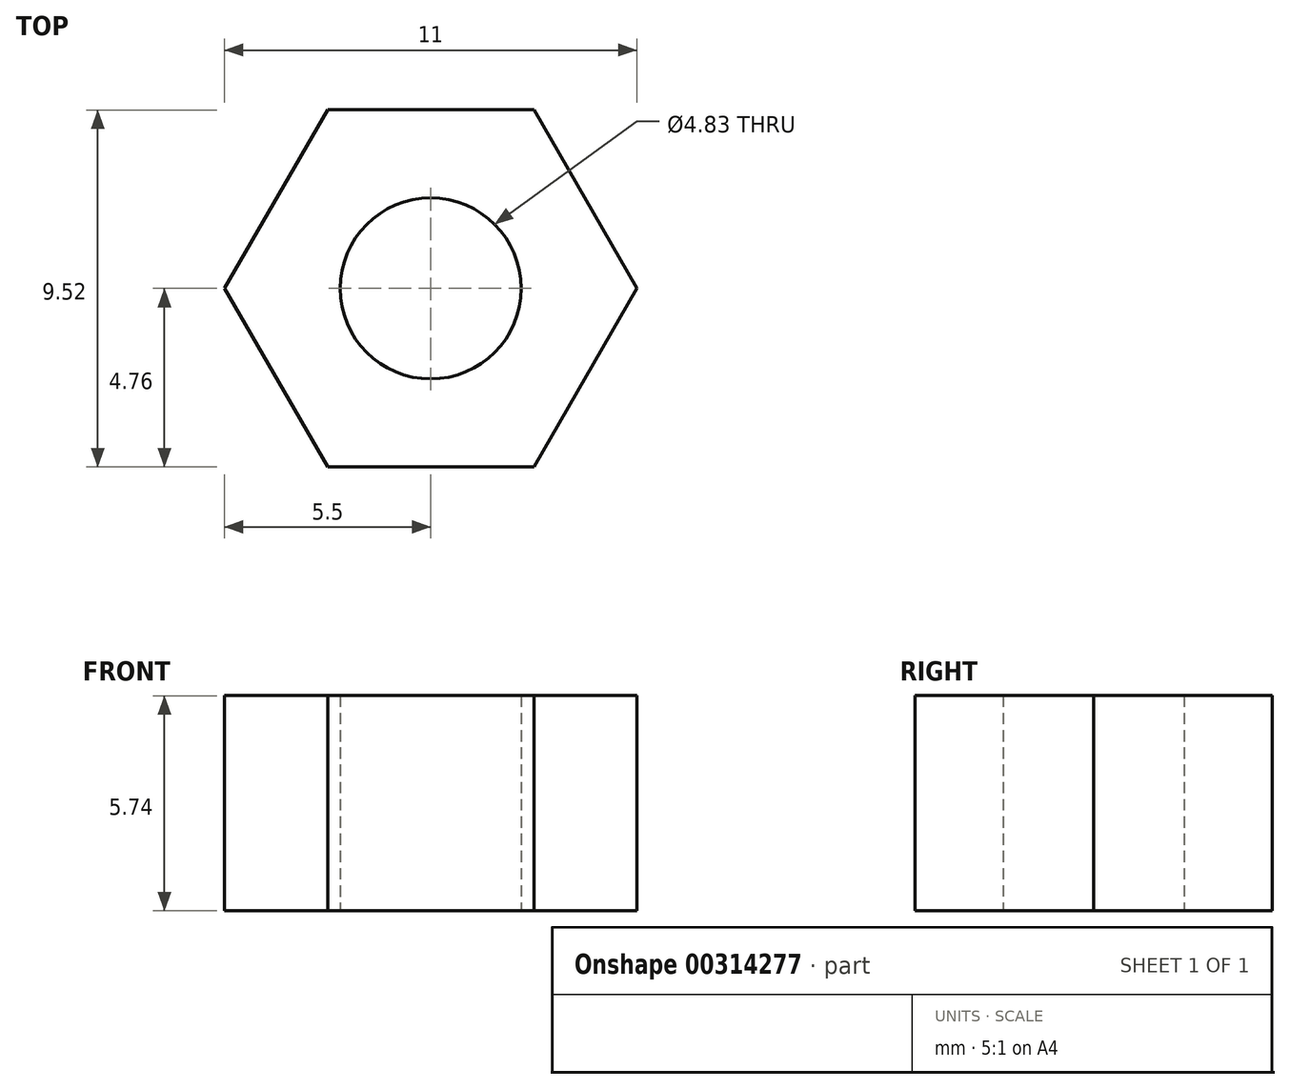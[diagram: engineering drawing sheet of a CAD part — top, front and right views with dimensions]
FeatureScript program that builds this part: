
annotation { "Feature Type Name" : "Feature", "Feature Type Description" : "" }
export const myFeature = defineFeature(function(context is Context, id is Id, definition is map)
    precondition{}
    {
        {
            var Q0;
            Q0=qCreatedBy(makeId("Top.planeOp"),FACE);
            var sketch = newSketch(context, id + "F0", { "sketchPlane" : qUnion([Q0])});
            skCircle(sketch, "E0.cCircle", {"center": v(0, 0) * mm, "radius": 4.76 * mm, "construction": true});
            skLineSegment(sketch, "E0.0", {"start": v(2.75, 4.76) * mm, "end": v(5.5, 0) * mm});
            skLineSegment(sketch, "E0.1", {"start": v(5.5, 0) * mm, "end": v(2.75, -4.76) * mm});
            skLineSegment(sketch, "E0.2", {"start": v(2.75, -4.76) * mm, "end": v(-2.75, -4.76) * mm});
            skLineSegment(sketch, "E0.3", {"start": v(-2.75, -4.76) * mm, "end": v(-5.5, 0) * mm});
            skLineSegment(sketch, "E0.4", {"start": v(-5.5, 0) * mm, "end": v(-2.75, 4.76) * mm});
            skLineSegment(sketch, "E0.5", {"start": v(-2.75, 4.76) * mm, "end": v(2.75, 4.76) * mm});
            skPoint(sketch, "E0.0.midPoint", {"position": v(4.12, 2.38) * mm});
            skSolve(sketch);
        }
        {
            var Q0;
            Q0=qSketchRegion(id+"F0",true);
            extrude(context, id + "F1", {"entities" : qUnion([Q0]), "depth" : 5.74 * mm});
        }
        {
            var Q0;
            Q0=sQuery(id+"F0.wireOp",VERTEX,"E0.cCircle.center");
            var Q1;
            Q1=makeQuery(id+"F1.opExtrude","SWEPT_BODY",BODY,{"disambiguationData":[OSD([sQuery(id+"F0.wireOp",EDGE,"E0.0"),sQuery(id+"F0.wireOp",EDGE,"E0.1"),sQuery(id+"F0.wireOp",EDGE,"E0.2"),sQuery(id+"F0.wireOp",EDGE,"E0.3"),sQuery(id+"F0.wireOp",EDGE,"E0.4"),sQuery(id+"F0.wireOp",EDGE,"E0.5")])]});
            hole(context, id + "F2", {"style" : HoleStyle.SIMPLE, "holeDiameter" : 4.83 * mm, "endStyle" : HoleEndStyle.THROUGH, "oppositeDirection" : true, "locations" : qUnion([Q0]), "scope" : qUnion([Q1])});
        }
    });
